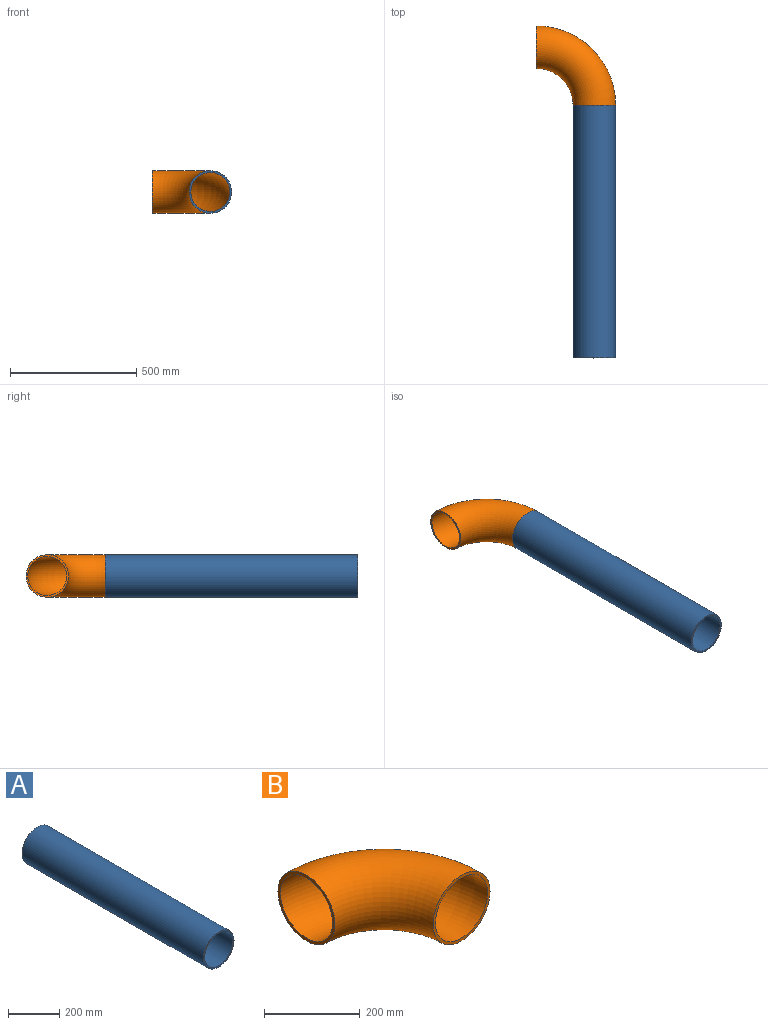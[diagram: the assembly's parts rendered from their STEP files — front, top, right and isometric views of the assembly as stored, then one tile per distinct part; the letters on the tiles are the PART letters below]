
ASSEMBLY  parts=2 mates=1
PART A: 4 faces, bbox 168.3x1000x168.3 mm
  f0: cylinder r=77.05mm len=1000mm, axis (0,-1,0), area 484119.4mm2, adj f2,f3
  f1: cylinder r=84.15mm len=1000mm, axis (0,-1,0), area 528730mm2, adj f2,f3
  f2: plane 168.3x168.3mm, normal (0,1,0), area 3595.6mm2, adj f0,f1
  f3: plane 168.3x168.3mm, normal (0,-1,0), area 3595.6mm2, adj f0,f1
PART B: 4 faces, bbox 339x339x168.3 mm
  f0: torus R=229mm, axis (0,0,1), area 174143.7mm2, adj f1,f2
  f1: plane 168.3x168.3mm, normal (0,-1,0), area 3595.6mm2, adj f0,f3
  f2: plane 168.3x168.3mm, normal (-1,0,0), area 3595.6mm2, adj f0,f3
  f3: torus R=229mm, axis (0,0,1), area 190190.7mm2, adj f1,f2
PLACE A t=(78.71,-725.61,264.79)mm
PLACE B t=(78.71,274.39,-35.21)mm
MATE fastened A.f0 <-> B.f1  axis (0,1,0) through (513.13,274.39,264.79)mm
